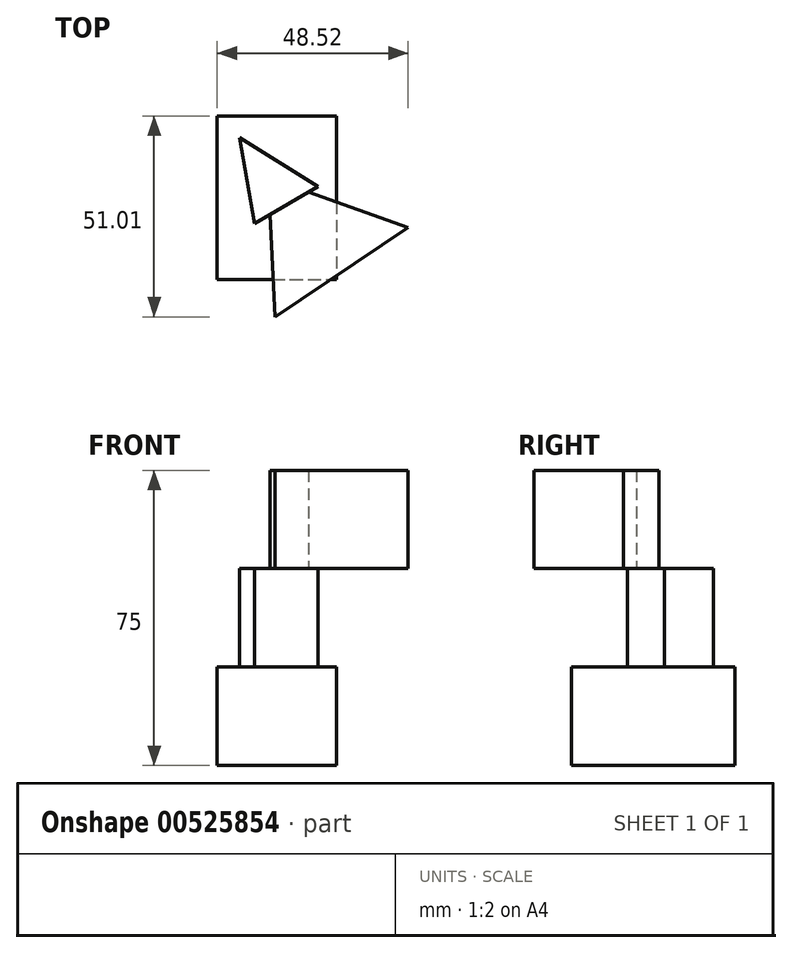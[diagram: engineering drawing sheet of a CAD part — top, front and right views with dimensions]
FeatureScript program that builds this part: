
annotation { "Feature Type Name" : "Feature", "Feature Type Description" : "" }
export const myFeature = defineFeature(function(context is Context, id is Id, definition is map)
    precondition{}
    {
        {
            var Q0;
            Q0=qCreatedBy(makeId("Top.planeOp"),FACE);
            var sketch = newSketch(context, id + "F0", { "sketchPlane" : qUnion([Q0])});
            skLineSegment(sketch, "E0.bottom", {"start": v(-34.09, 46.16) * mm, "end": v(-3.73, 46.16) * mm});
            skLineSegment(sketch, "E0.top", {"start": v(-34.09, 4.6) * mm, "end": v(-3.73, 4.6) * mm});
            skLineSegment(sketch, "E0.left", {"start": v(-34.09, 46.16) * mm, "end": v(-34.09, 4.6) * mm});
            skLineSegment(sketch, "E0.right", {"start": v(-3.73, 46.16) * mm, "end": v(-3.73, 4.6) * mm});
            skLineSegment(sketch, "E1.bottom", {"start": v(9.95, 44.66) * mm, "end": v(44.29, 44.66) * mm});
            skLineSegment(sketch, "E1.top", {"start": v(9.95, 0) * mm, "end": v(44.29, 0) * mm});
            skLineSegment(sketch, "E1.left", {"start": v(9.95, 44.66) * mm, "end": v(9.95, 0) * mm});
            skLineSegment(sketch, "E1.right", {"start": v(44.29, 44.66) * mm, "end": v(44.29, 0) * mm});
            skLineSegment(sketch, "E2.bottom", {"start": v(-36.08, -12.57) * mm, "end": v(-10.45, -12.57) * mm});
            skLineSegment(sketch, "E2.top", {"start": v(-36.08, -34.96) * mm, "end": v(-10.45, -34.96) * mm});
            skLineSegment(sketch, "E2.left", {"start": v(-36.08, -12.57) * mm, "end": v(-36.08, -34.96) * mm});
            skLineSegment(sketch, "E2.right", {"start": v(-10.45, -12.57) * mm, "end": v(-10.45, -34.96) * mm});
            skLineSegment(sketch, "E3.bottom", {"start": v(-10.45, -27.25) * mm, "end": v(15.92, -27.25) * mm});
            skLineSegment(sketch, "E3.top", {"start": v(-10.45, -53.37) * mm, "end": v(15.92, -53.37) * mm});
            skLineSegment(sketch, "E3.left", {"start": v(-10.45, -27.25) * mm, "end": v(-10.45, -53.37) * mm});
            skLineSegment(sketch, "E3.right", {"start": v(15.92, -27.25) * mm, "end": v(15.92, -53.37) * mm});
            skPoint(sketch, "E4.oppositeSnap0", {"position": v(15.92, -40.3) * mm});
            skLineSegment(sketch, "E4.bottom", {"start": v(18.41, -16.05) * mm, "end": v(44.29, -16.05) * mm});
            skLineSegment(sketch, "E4.top", {"start": v(18.41, -40.3) * mm, "end": v(44.29, -40.3) * mm});
            skLineSegment(sketch, "E4.left", {"start": v(18.41, -16.05) * mm, "end": v(18.41, -40.3) * mm});
            skLineSegment(sketch, "E4.right", {"start": v(44.29, -16.05) * mm, "end": v(44.29, -40.3) * mm});
            skSolve(sketch);
        }
        {
            var Q0;
            Q0=makeQuery(id+"F0.imprint","IMPRINT",FACE,{"disambiguationData":[TD([[makeQuery(id+"F0.imprint","IMPRINT",EDGE,{"derivedFrom":sQuery(id+"F0.wireOp",EDGE,"E0.bottom")}),-1.0]])]});
            extrude(context, id + "F1", {"entities" : qUnion([Q0]), "depth" : 25 * mm, "offsetDistance" : 25 * mm});
        }
        {
            var Q0;
            Q0=makeQuery(id+"F1.opExtrude","CAP_FACE",FACE,{"disambiguationData":[OSD([sQuery(id+"F0.wireOp",EDGE,"E0.bottom"),sQuery(id+"F0.wireOp",EDGE,"E0.top"),sQuery(id+"F0.wireOp",EDGE,"E0.left"),sQuery(id+"F0.wireOp",EDGE,"E0.right")])],"isStart":false});
            var sketch = newSketch(context, id + "F2", { "sketchPlane" : qUnion([Q0])});
            skLineSegment(sketch, "E5", {"start": v(-28.36, 40.68) * mm, "end": v(-8.46, 28.24) * mm});
            skLineSegment(sketch, "E6", {"start": v(-8.46, 28.24) * mm, "end": v(-24.63, 18.79) * mm});
            skLineSegment(sketch, "E7", {"start": v(-24.63, 18.79) * mm, "end": v(-28.36, 40.68) * mm});
            skSolve(sketch);
        }
        {
            var Q0;
            Q0=makeQuery(id+"F2.imprint","IMPRINT",FACE,{"disambiguationData":[TD([[makeQuery(id+"F2.imprint","IMPRINT",EDGE,{"derivedFrom":sQuery(id+"F2.wireOp",EDGE,"E5")}),-1.0]])]});
            extrude(context, id + "F3", {"entities" : qUnion([Q0]), "operationType" : NewBodyOperationType.ADD, "depth" : 25 * mm, "offsetDistance" : 25 * mm});
        }
        {
            var Q0;
            Q0=makeQuery(id+"F3.opExtrude","CAP_FACE",FACE,{"disambiguationData":[OSD([sQuery(id+"F2.wireOp",EDGE,"E5"),sQuery(id+"F2.wireOp",EDGE,"E6"),sQuery(id+"F2.wireOp",EDGE,"E7")])],"isStart":false});
            var sketch = newSketch(context, id + "F4", { "sketchPlane" : qUnion([Q0])});
            skLineSegment(sketch, "E8", {"start": v(-21.15, 30.48) * mm, "end": v(14.43, 17.8) * mm});
            skLineSegment(sketch, "E9", {"start": v(14.43, 17.8) * mm, "end": v(-19.4, -4.85) * mm});
            skLineSegment(sketch, "E10", {"start": v(-19.4, -4.85) * mm, "end": v(-21.15, 30.48) * mm});
            skSolve(sketch);
        }
        {
            var Q0;
            {var subQ0=sQuery(id+"F4.wireOp",EDGE,"E9");Q0=makeQuery(id+"F4.imprint","IMPRINT",FACE,{"disambiguationData":[TD([[makeQuery(id+"F4.imprint","IMPRINT",EDGE,{"derivedFrom":subQ0}),-1.0]])]});}
            extrude(context, id + "F5", {"entities" : qUnion([Q0]), "depth" : 25 * mm, "offsetDistance" : 25 * mm});
        }
    });
